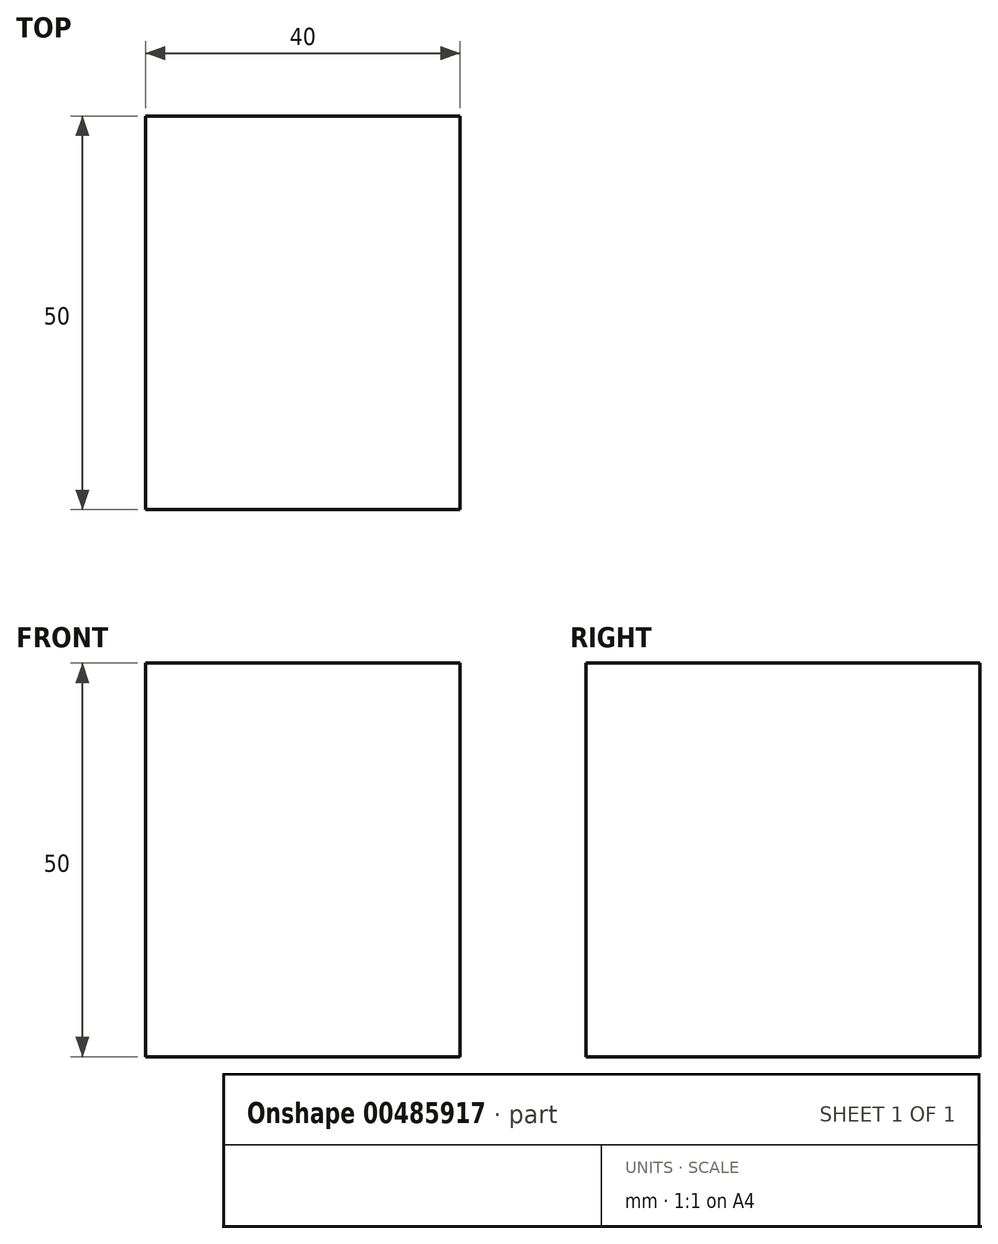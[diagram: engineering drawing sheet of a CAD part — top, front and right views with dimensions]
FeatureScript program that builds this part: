
annotation { "Feature Type Name" : "Feature", "Feature Type Description" : "" }
export const myFeature = defineFeature(function(context is Context, id is Id, definition is map)
    precondition{}
    {
        {
            var Q0;
            Q0=qCreatedBy(makeId("Top.planeOp"),FACE);
            var sketch = newSketch(context, id + "F0", { "sketchPlane" : qUnion([Q0])});
            skLineSegment(sketch, "E0.bottom", {"start": v(-20, 50) * mm, "end": v(0, 50) * mm});
            skLineSegment(sketch, "E0.top", {"start": v(-20, 0) * mm, "end": v(0, 0) * mm});
            skLineSegment(sketch, "E0.left", {"start": v(-20, 50) * mm, "end": v(-20, 0) * mm});
            skLineSegment(sketch, "E0.right", {"start": v(0, 50) * mm, "end": v(0, 0) * mm, "construction": true});
            skLineSegment(sketch, "E1.MirrorCS", {"start": v(20, 0) * mm, "end": v(0, 0) * mm});
            skLineSegment(sketch, "E2.MirrorCS", {"start": v(20, 50) * mm, "end": v(0, 50) * mm});
            skLineSegment(sketch, "E3.MirrorCS", {"start": v(20, 50) * mm, "end": v(20, 0) * mm});
            skSolve(sketch);
        }
        {
            var Q0;
            Q0=makeQuery(id+"F0.imprint","IMPRINT",FACE,{"disambiguationData":[TD([[makeQuery(id+"F0.imprint","IMPRINT",EDGE,{"derivedFrom":sQuery(id+"F0.wireOp",EDGE,"E0.bottom")}),-1.0]])]});
            extrude(context, id + "F1", {"entities" : qUnion([Q0]), "endBound" : BoundingType.SYMMETRIC, "depth" : 50 * mm});
        }
    });
